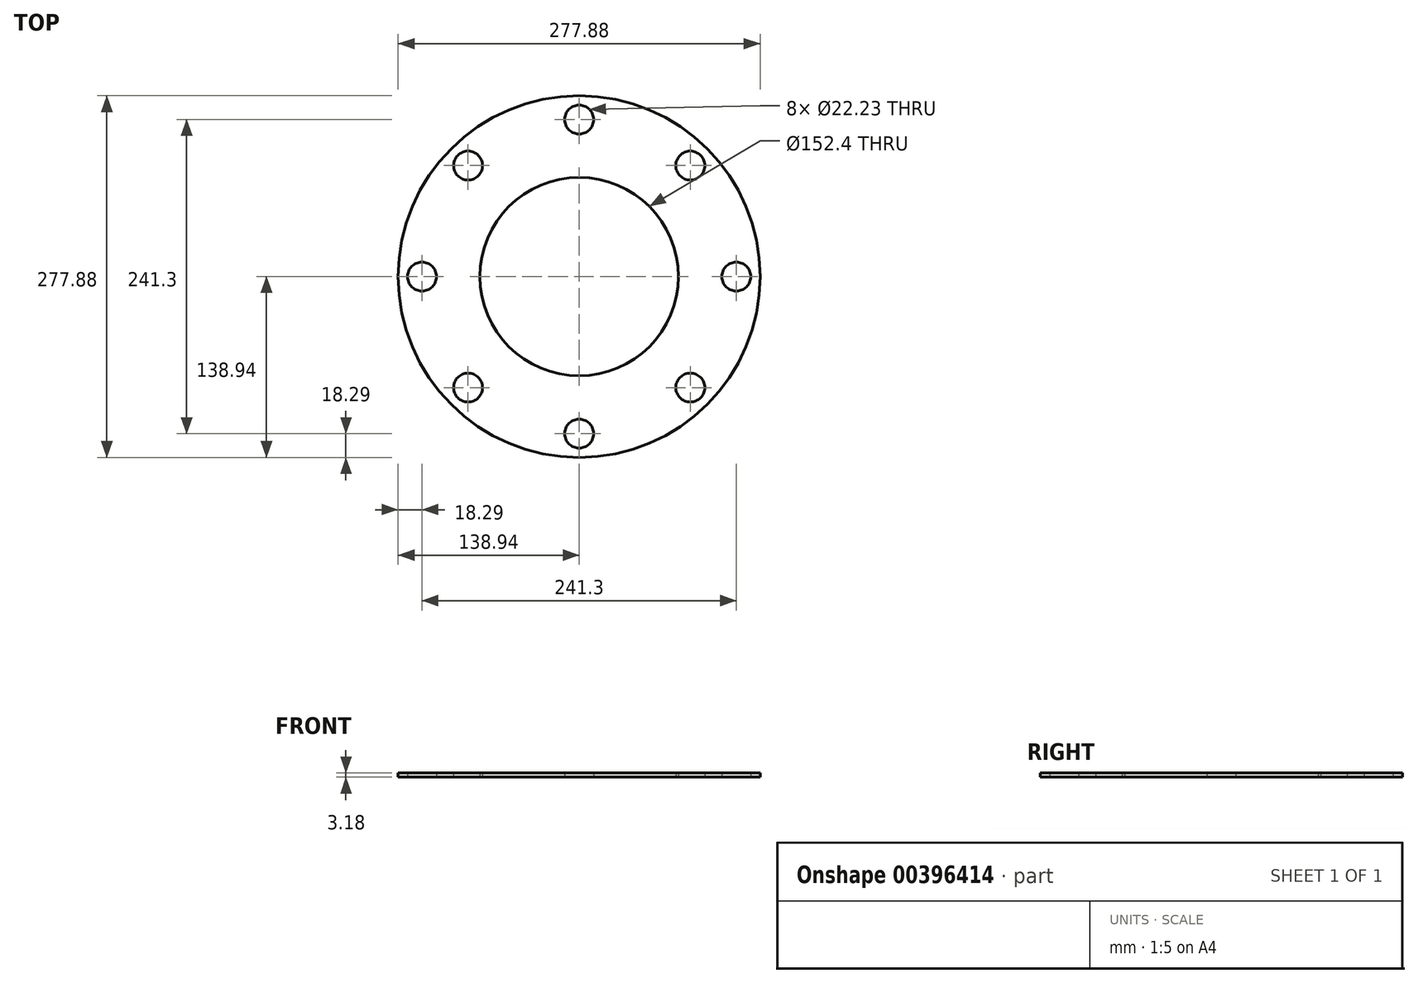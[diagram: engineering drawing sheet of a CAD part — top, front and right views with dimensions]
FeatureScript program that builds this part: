
annotation { "Feature Type Name" : "Feature", "Feature Type Description" : "" }
export const myFeature = defineFeature(function(context is Context, id is Id, definition is map)
    precondition{}
    {
        {
            var Q0;
            Q0=qCreatedBy(makeId("Top.planeOp"),FACE);
            var sketch = newSketch(context, id + "F0", { "sketchPlane" : qUnion([Q0])});
            skCircle(sketch, "E0", {"center": v(0, 0) * mm, "radius": 138.94 * mm});
            skCircle(sketch, "E1", {"center": v(0, 0) * mm, "radius": 76.2 * mm});
            skCircle(sketch, "E2", {"center": v(0, 0) * mm, "radius": 120.65 * mm, "construction": true});
            skPoint(sketch, "E3", {"position": v(0, 120.65) * mm});
            skPoint(sketch, "E4", {"position": v(-120.65, 0) * mm});
            skPoint(sketch, "E5", {"position": v(0, -120.65) * mm});
            skPoint(sketch, "E6", {"position": v(120.65, 0) * mm});
            skPoint(sketch, "E7", {"position": v(85.31, 85.31) * mm});
            skPoint(sketch, "E8", {"position": v(85.31, -85.31) * mm});
            skPoint(sketch, "E9", {"position": v(-85.31, -85.31) * mm});
            skPoint(sketch, "E10", {"position": v(-85.31, 85.31) * mm});
            skLineSegment(sketch, "E11", {"start": v(0, 0) * mm, "end": v(-121.31, 121.31) * mm, "construction": true});
            skSolve(sketch);
        }
        {
            var Q0;
            Q0=makeQuery(id+"F0.imprint","IMPRINT",FACE,{"disambiguationData":[TD([[makeQuery(id+"F0.imprint","IMPRINT",EDGE,{"derivedFrom":sQuery(id+"F0.wireOp",EDGE,"E0")}),1.0]])]});
            extrude(context, id + "F1", {"entities" : qUnion([Q0]), "depth" : 3.17 * mm});
        }
        {
            var Q0;
            Q0=sQuery(id+"F0.wireOp",VERTEX,"E10");
            var Q1;
            Q1=sQuery(id+"F0.wireOp",VERTEX,"E4");
            var Q2;
            Q2=sQuery(id+"F0.wireOp",VERTEX,"E9");
            var Q3;
            Q3=sQuery(id+"F0.wireOp",VERTEX,"E5");
            var Q4;
            Q4=sQuery(id+"F0.wireOp",VERTEX,"E8");
            var Q5;
            Q5=sQuery(id+"F0.wireOp",VERTEX,"E6");
            var Q6;
            Q6=sQuery(id+"F0.wireOp",VERTEX,"E7");
            var Q7;
            Q7=sQuery(id+"F0.wireOp",VERTEX,"E3");
            var Q8;
            Q8=makeQuery(id+"F1.opExtrude","SWEPT_BODY",BODY,{"disambiguationData":[OSD([sQuery(id+"F0.wireOp",EDGE,"E0"),sQuery(id+"F0.wireOp",EDGE,"E1")])]});
            hole(context, id + "F2", {"style" : HoleStyle.SIMPLE, "endStyle" : HoleEndStyle.THROUGH, "oppositeDirection" : true, "holeDiameter" : 22.22 * mm, "isTappedThrough" : true, "tappedDepth" : 12.7 * mm, "tapClearance" : 3, "locations" : qUnion([Q0, Q1, Q2, Q3, Q4, Q5, Q6, Q7]), "scope" : qUnion([Q8])});
        }
    });
